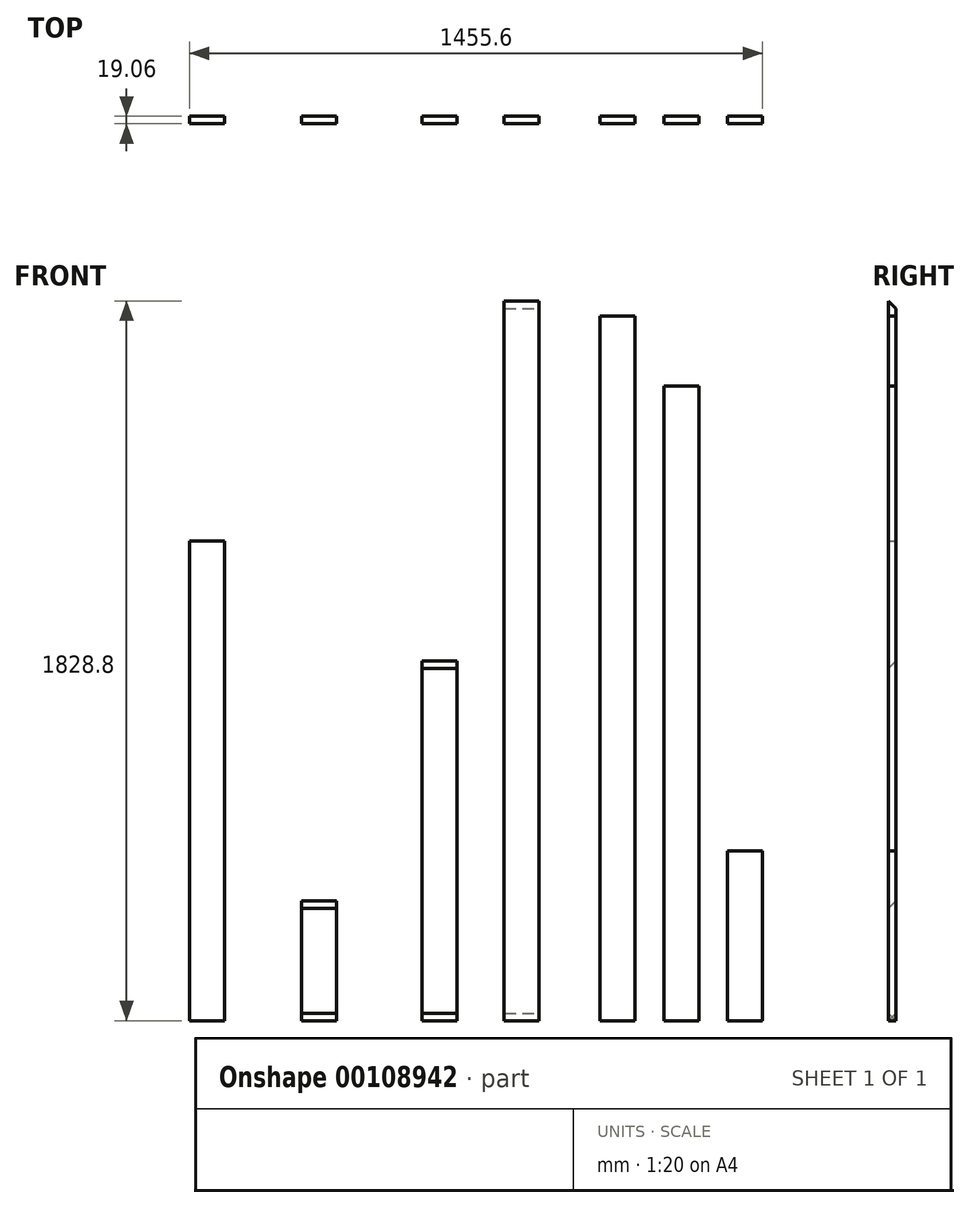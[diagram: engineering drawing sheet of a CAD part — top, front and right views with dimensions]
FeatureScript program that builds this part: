
annotation { "Feature Type Name" : "Feature", "Feature Type Description" : "" }
export const myFeature = defineFeature(function(context is Context, id is Id, definition is map)
    precondition{}
    {
        {
            var Q0;
            Q0=qCreatedBy(makeId("Top.planeOp"),FACE);
            var sketch = newSketch(context, id + "F0", { "sketchPlane" : qUnion([Q0])});
            skLineSegment(sketch, "E0.bottom", {"start": v(44.45, -9.52) * mm, "end": v(-44.45, -9.53) * mm});
            skLineSegment(sketch, "E0.top", {"start": v(44.45, 9.53) * mm, "end": v(-44.45, 9.53) * mm});
            skLineSegment(sketch, "E0.left", {"start": v(44.45, -9.52) * mm, "end": v(44.45, 9.53) * mm});
            skLineSegment(sketch, "E0.right", {"start": v(-44.45, -9.53) * mm, "end": v(-44.45, 9.53) * mm});
            skPoint(sketch, "E0.middle", {"position": v(0, 0) * mm});
            skSolve(sketch);
        }
        {
            var Q0;
            Q0=makeQuery(id+"F0.imprint","IMPRINT",FACE,{"disambiguationData":[TD([[makeQuery(id+"F0.imprint","IMPRINT",EDGE,{"derivedFrom":sQuery(id+"F0.wireOp",EDGE,"E0.bottom")}),-1.0]])]});
            extrude(context, id + "F1", {"entities" : qUnion([Q0]), "depth" : 1828.8 * mm});
        }
        {
            var Q0;
            Q0=makeQuery(id+"F1.opExtrude","SWEPT_FACE",FACE,{"disambiguationData":[OSD([sQuery(id+"F0.wireOp",EDGE,"E0.left")])]});
            var sketch = newSketch(context, id + "F2", { "sketchPlane" : qUnion([Q0])});
            skLineSegment(sketch, "E1", {"start": v(-9.52, 1828.8) * mm, "end": v(9.53, 1809.75) * mm});
            skLineSegment(sketch, "E2", {"start": v(-9.52, 0) * mm, "end": v(9.53, 19.05) * mm});
            skSolve(sketch);
        }
        {
            var Q0;
            {var subQ0=sQuery(id+"F2.wireOp",EDGE,"E1");Q0=makeQuery(id+"F2.imprint","IMPRINT",FACE,{"disambiguationData":[TD([[makeQuery(id+"F2.imprint","IMPRINT",EDGE,{"derivedFrom":subQ0}),1.0]])]});}
            var Q1;
            {var subQ0=sQuery(id+"F2.wireOp",EDGE,"E2");Q1=makeQuery(id+"F2.imprint","IMPRINT",FACE,{"disambiguationData":[TD([[makeQuery(id+"F2.imprint","IMPRINT",EDGE,{"derivedFrom":subQ0}),-1.0]])]});}
            extrude(context, id + "F3", {"entities" : qUnion([Q0, Q1]), "operationType" : NewBodyOperationType.REMOVE, "oppositeDirection" : true, "depth" : 413.46 * mm});
        }
        {
            var Q0;
            Q0=qCreatedBy(makeId("Top.planeOp"),FACE);
            var sketch = newSketch(context, id + "F4", { "sketchPlane" : qUnion([Q0])});
            skLineSegment(sketch, "E3.bottom", {"start": v(-164.69, -9.52) * mm, "end": v(-253.59, -9.52) * mm});
            skLineSegment(sketch, "E3.top", {"start": v(-164.69, 9.53) * mm, "end": v(-253.59, 9.53) * mm});
            skLineSegment(sketch, "E3.left", {"start": v(-164.69, -9.52) * mm, "end": v(-164.69, 9.53) * mm});
            skLineSegment(sketch, "E3.right", {"start": v(-253.59, -9.52) * mm, "end": v(-253.59, 9.53) * mm});
            skPoint(sketch, "E3.middle", {"position": v(-209.14, 0) * mm});
            skSolve(sketch);
        }
        {
            var Q0;
            Q0=makeQuery(id+"F4.imprint","IMPRINT",FACE,{"disambiguationData":[TD([[makeQuery(id+"F4.imprint","IMPRINT",EDGE,{"derivedFrom":sQuery(id+"F4.wireOp",EDGE,"E3.bottom")}),-1.0]])]});
            extrude(context, id + "F5", {"entities" : qUnion([Q0]), "depth" : 914.4 * mm});
        }
        {
            var Q0;
            Q0=makeQuery(id+"F5.opExtrude","SWEPT_FACE",FACE,{"disambiguationData":[OSD([sQuery(id+"F4.wireOp",EDGE,"E3.right")])]});
            var sketch = newSketch(context, id + "F6", { "sketchPlane" : qUnion([Q0])});
            skLineSegment(sketch, "E4", {"start": v(-9.52, 914.4) * mm, "end": v(9.53, 895.35) * mm});
            skLineSegment(sketch, "E5", {"start": v(-9.52, 0) * mm, "end": v(9.52, 19.05) * mm});
            skSolve(sketch);
        }
        {
            var Q0;
            {var subQ0=sQuery(id+"F6.wireOp",EDGE,"E4");Q0=makeQuery(id+"F6.imprint","IMPRINT",FACE,{"disambiguationData":[TD([[makeQuery(id+"F6.imprint","IMPRINT",EDGE,{"derivedFrom":subQ0}),1.0]])]});}
            var Q1;
            {var subQ0=sQuery(id+"F6.wireOp",EDGE,"E5");Q1=makeQuery(id+"F6.imprint","IMPRINT",FACE,{"disambiguationData":[TD([[makeQuery(id+"F6.imprint","IMPRINT",EDGE,{"derivedFrom":subQ0}),-1.0]])]});}
            extrude(context, id + "F7", {"entities" : qUnion([Q0, Q1]), "operationType" : NewBodyOperationType.REMOVE, "oppositeDirection" : true, "depth" : 204.4 * mm});
        }
        {
            var Q0;
            Q0=qCreatedBy(makeId("Top.planeOp"),FACE);
            var sketch = newSketch(context, id + "F8", { "sketchPlane" : qUnion([Q0])});
            skLineSegment(sketch, "E6.bottom", {"start": v(198.69, -9.53) * mm, "end": v(287.59, -9.52) * mm});
            skLineSegment(sketch, "E6.top", {"start": v(198.69, 9.52) * mm, "end": v(287.59, 9.53) * mm});
            skLineSegment(sketch, "E6.left", {"start": v(198.69, -9.53) * mm, "end": v(198.69, 9.52) * mm});
            skLineSegment(sketch, "E6.right", {"start": v(287.59, -9.53) * mm, "end": v(287.59, 9.52) * mm});
            skPoint(sketch, "E6.middle", {"position": v(243.14, 0) * mm});
            skSolve(sketch);
        }
        {
            var Q0;
            Q0=makeQuery(id+"F8.imprint","IMPRINT",FACE,{"disambiguationData":[TD([[makeQuery(id+"F8.imprint","IMPRINT",EDGE,{"derivedFrom":sQuery(id+"F8.wireOp",EDGE,"E6.bottom")}),1.0]])]});
            extrude(context, id + "F9", {"entities" : qUnion([Q0]), "depth" : 1790.7 * mm});
        }
        {
            var Q0;
            Q0=qCreatedBy(makeId("Top.planeOp"),FACE);
            var sketch = newSketch(context, id + "F10", { "sketchPlane" : qUnion([Q0])});
            skLineSegment(sketch, "E7.bottom", {"start": v(-469.86, -9.52) * mm, "end": v(-558.76, -9.52) * mm});
            skLineSegment(sketch, "E7.top", {"start": v(-469.86, 9.53) * mm, "end": v(-558.76, 9.53) * mm});
            skLineSegment(sketch, "E7.left", {"start": v(-469.86, -9.52) * mm, "end": v(-469.86, 9.53) * mm});
            skLineSegment(sketch, "E7.right", {"start": v(-558.76, -9.52) * mm, "end": v(-558.76, 9.53) * mm});
            skPoint(sketch, "E7.middle", {"position": v(-514.31, 0) * mm});
            skSolve(sketch);
        }
        {
            var Q0;
            Q0=makeQuery(id+"F10.imprint","IMPRINT",FACE,{"disambiguationData":[TD([[makeQuery(id+"F10.imprint","IMPRINT",EDGE,{"derivedFrom":sQuery(id+"F10.wireOp",EDGE,"E7.bottom")}),-1.0]])]});
            extrude(context, id + "F11", {"entities" : qUnion([Q0]), "depth" : 304.8 * mm});
        }
        {
            var Q0;
            Q0=makeQuery(id+"F11.opExtrude","SWEPT_FACE",FACE,{"disambiguationData":[OSD([sQuery(id+"F10.wireOp",EDGE,"E7.right")])]});
            var sketch = newSketch(context, id + "F12", { "sketchPlane" : qUnion([Q0])});
            skLineSegment(sketch, "E8", {"start": v(-9.52, 304.8) * mm, "end": v(9.53, 285.75) * mm});
            skLineSegment(sketch, "E9", {"start": v(-9.52, 0) * mm, "end": v(9.53, 19.05) * mm});
            skSolve(sketch);
        }
        {
            var Q0;
            {var subQ0=sQuery(id+"F12.wireOp",EDGE,"E9");Q0=makeQuery(id+"F12.imprint","IMPRINT",FACE,{"disambiguationData":[TD([[makeQuery(id+"F12.imprint","IMPRINT",EDGE,{"derivedFrom":subQ0}),-1.0]])]});}
            var Q1;
            {var subQ0=sQuery(id+"F12.wireOp",EDGE,"E8");Q1=makeQuery(id+"F12.imprint","IMPRINT",FACE,{"disambiguationData":[TD([[makeQuery(id+"F12.imprint","IMPRINT",EDGE,{"derivedFrom":subQ0}),1.0]])]});}
            extrude(context, id + "F13", {"entities" : qUnion([Q0, Q1]), "operationType" : NewBodyOperationType.REMOVE, "oppositeDirection" : true, "depth" : 205.58 * mm});
        }
        {
            var Q0;
            Q0=qCreatedBy(makeId("Top.planeOp"),FACE);
            var sketch = newSketch(context, id + "F14", { "sketchPlane" : qUnion([Q0])});
            skLineSegment(sketch, "E10.bottom", {"start": v(361.33, -9.53) * mm, "end": v(450.23, -9.53) * mm});
            skLineSegment(sketch, "E10.top", {"start": v(361.33, 9.52) * mm, "end": v(450.23, 9.52) * mm});
            skLineSegment(sketch, "E10.left", {"start": v(361.33, -9.53) * mm, "end": v(361.33, 9.52) * mm});
            skLineSegment(sketch, "E10.right", {"start": v(450.23, -9.53) * mm, "end": v(450.23, 9.52) * mm});
            skPoint(sketch, "E10.middle", {"position": v(405.78, 0) * mm});
            skSolve(sketch);
        }
        {
            var Q0;
            Q0=makeQuery(id+"F14.imprint","IMPRINT",FACE,{"disambiguationData":[TD([[makeQuery(id+"F14.imprint","IMPRINT",EDGE,{"derivedFrom":sQuery(id+"F14.wireOp",EDGE,"E10.bottom")}),1.0]])]});
            extrude(context, id + "F15", {"entities" : qUnion([Q0]), "depth" : 1612.9 * mm});
        }
        {
            var Q0;
            Q0=qCreatedBy(makeId("Top.planeOp"),FACE);
            var sketch = newSketch(context, id + "F16", { "sketchPlane" : qUnion([Q0])});
            skLineSegment(sketch, "E11.bottom", {"start": v(-754.87, -9.52) * mm, "end": v(-843.77, -9.52) * mm});
            skLineSegment(sketch, "E11.top", {"start": v(-754.87, 9.53) * mm, "end": v(-843.77, 9.53) * mm});
            skLineSegment(sketch, "E11.left", {"start": v(-754.87, -9.52) * mm, "end": v(-754.87, 9.53) * mm});
            skLineSegment(sketch, "E11.right", {"start": v(-843.77, -9.52) * mm, "end": v(-843.77, 9.53) * mm});
            skPoint(sketch, "E11.middle", {"position": v(-799.32, 0) * mm});
            skSolve(sketch);
        }
        {
            var Q0;
            Q0=makeQuery(id+"F16.imprint","IMPRINT",FACE,{"disambiguationData":[TD([[makeQuery(id+"F16.imprint","IMPRINT",EDGE,{"derivedFrom":sQuery(id+"F16.wireOp",EDGE,"E11.bottom")}),-1.0]])]});
            extrude(context, id + "F17", {"entities" : qUnion([Q0]), "depth" : 1219.2 * mm});
        }
        {
            var Q0;
            Q0=qCreatedBy(makeId("Top.planeOp"),FACE);
            var sketch = newSketch(context, id + "F18", { "sketchPlane" : qUnion([Q0])});
            skLineSegment(sketch, "E12.bottom", {"start": v(522.93, -9.53) * mm, "end": v(611.83, -9.53) * mm});
            skLineSegment(sketch, "E12.top", {"start": v(522.93, 9.53) * mm, "end": v(611.83, 9.53) * mm});
            skLineSegment(sketch, "E12.left", {"start": v(522.93, -9.53) * mm, "end": v(522.93, 9.53) * mm});
            skLineSegment(sketch, "E12.right", {"start": v(611.83, -9.53) * mm, "end": v(611.83, 9.53) * mm});
            skPoint(sketch, "E12.middle", {"position": v(567.38, 0) * mm});
            skSolve(sketch);
        }
        {
            var Q0;
            Q0=makeQuery(id+"F18.imprint","IMPRINT",FACE,{"disambiguationData":[TD([[makeQuery(id+"F18.imprint","IMPRINT",EDGE,{"derivedFrom":sQuery(id+"F18.wireOp",EDGE,"E12.bottom")}),1.0]])]});
            extrude(context, id + "F19", {"entities" : qUnion([Q0]), "depth" : 431.8 * mm});
        }
    });
